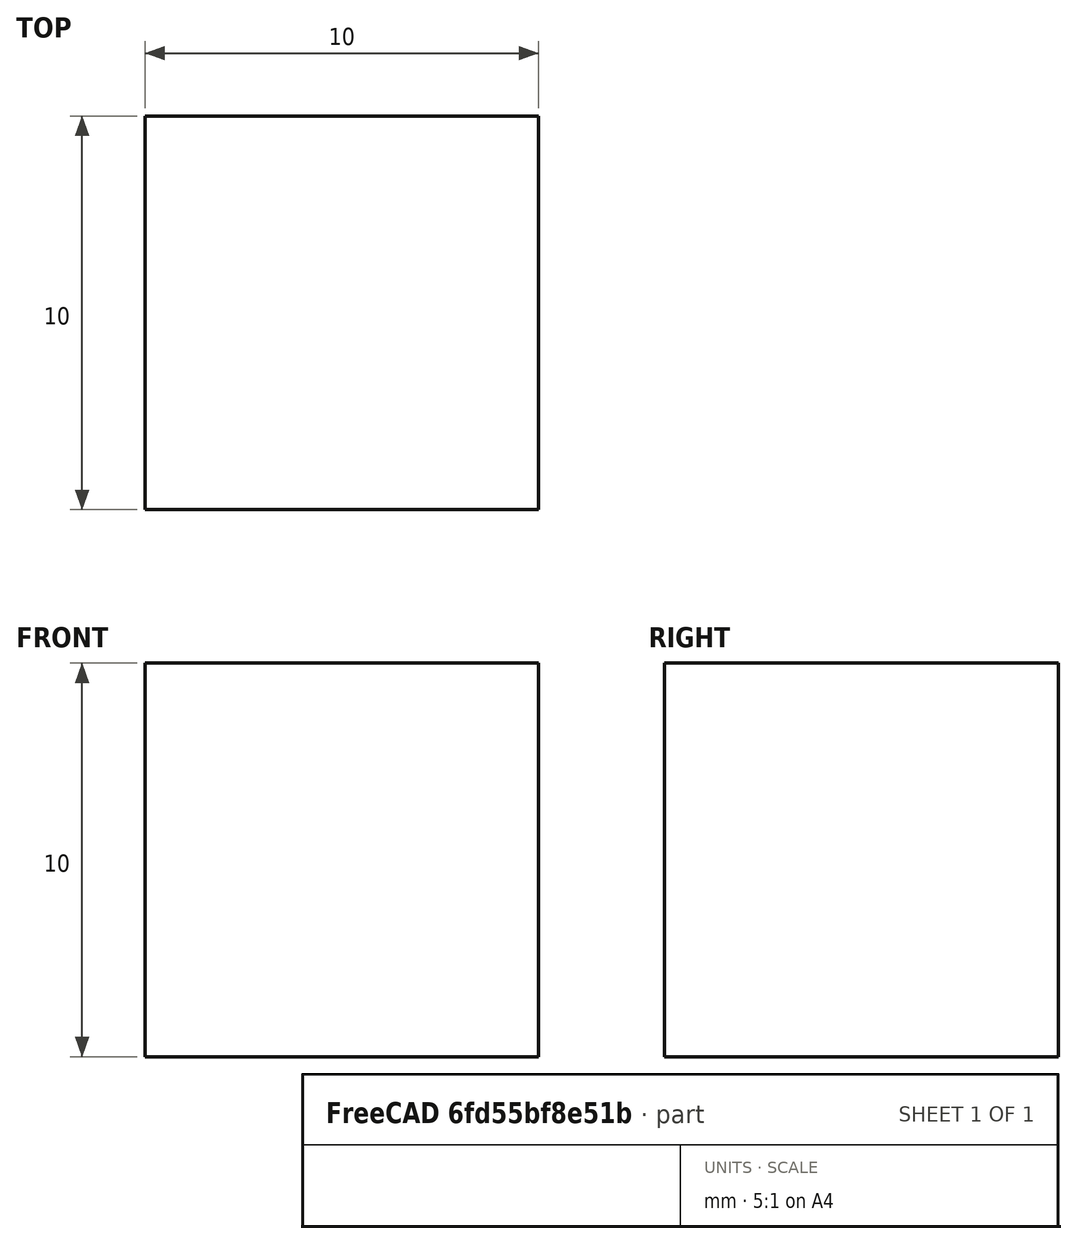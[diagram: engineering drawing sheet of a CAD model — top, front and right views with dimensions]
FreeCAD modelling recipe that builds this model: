
FCSTD DOCUMENT  (FreeCAD 1.0R39109 (Git))
Label: Simple Shear
License: All rights reserved
LicenseURL: http://en.wikipedia.org/wiki/All_rights_reserved
objects: Fem::ConstraintForce×4, Fem::ConstraintDisplacement×2, Part::Box×1, Fem::FemSolverObjectPython×1, App::MaterialObjectPython×1, Fem::FemMeshObjectPython×1, Fem::ConstraintFixed×1, Fem::FemAnalysis×1
note: 1 computed .brp shape members not serialized (recipe doc carries the construction recipe); baked Part::Feature solids carry a one-line shape summary decoded from their .brp

FEATURE [Part::Box] Box  label="Cube"
  AttacherType = Attacher::AttachEngine3D
  Height = 10
  Length = 10
  Width = 10
FEATURE [Fem::FemSolverObjectPython] SolverCcxTools  # FEM object (typed FeaturePython)
  AnalysisType = 0
  BeamReducedIntegration = true
  BeamShellResultOutput3D = false
  BucklingFactors = 1
  EigenmodeHighLimit = 1000000
  EigenmodeLowLimit = 0
  EigenmodesCount = 10
  GeometricalNonlinearity = 0
  IterationsControlParameterCutb = 0.25,0.5,0.75,0.85,,,1.5,
  IterationsControlParameterIter = 4,8,9,200,10,400,,200,,
  IterationsControlParameterTimeUse = false
  IterationsMaximum = 2000
  IterationsUserDefinedIncrementations = false
  IterationsUserDefinedTimeStepLength = false
  MaterialNonlinearity = 0
  MatrixSolverType = 0
  ModelSpace = 0
  OutputFrequency = 1
  SplitInputWriter = false
  ThermoMechSteadyState = true
  ThermoMechType = 0
  TimeEnd = 1
  TimeInitialStep = 0.01
  TimeMaximumStep = 1
  TimeMinimumStep = 1e-05
FEATURE [App::MaterialObjectPython] MaterialSolid  # material (typed FeaturePython)
  Category = 0
  Material = AuthorAndLicense=(c) 2013 Yorik van Havre (CC-BY 3.0); CardName=Concrete-Generic; CompressiveStrength=25 MPa; Density=2400 kg/m^3; Description=A standard C-25 construction concrete; Father=Aggregate; Name=Concrete; PoissonRatio=0.17; ProductURL=https://en.wikipedia.org/wiki/Concrete; StandardCode=Masterformat 03 33 13; YoungsModulus=32000 MPa
FEATURE [Fem::FemMeshObjectPython] FEMMeshGmsh  # FEM object (typed FeaturePython)
  Algorithm2D = 0
  Algorithm3D = 0
  CharacteristicLengthMax = 0
  CharacteristicLengthMin = 10
  CoherenceMesh = true
  ElementDimension = 0
  ElementOrder = 1
  GeometryTolerance = 1e-06
  GroupsOfNodes = false
  HighOrderOptimize = 0
  MeshSizeFromCurvature = 12
  OptimizeNetgen = false
  OptimizeStd = true
  RecombinationAlgorithm = 0
  Recombine3DAll = false
  RecombineAll = false
  SecondOrderLinear = false
  Shape = -> Box
  SubdivisionAlgorithm = 0
FEATURE [Fem::ConstraintForce] ConstraintForce
  Direction = -> Box [Edge10]
  DirectionVector = (1,0,0)
  Force = 100000
  NormalDirection = (0,0,1)
  Normals = (9) [(0,0,1),(0,0,1),(0,0,1),(0,0,1),(0,0,1),(0,0,1),(0,0,1),(0,0,1),(0,0,1)]
  Points = (9) [(0,0,10),(5,0,10),(10,0,10),(0,5,10),(5,5,10),(10,5,10),(0,10,10),(5,10,10),(10,10,10)]
  References = -> [Box]
  Suppressed = false
FEATURE [Fem::ConstraintForce] ConstraintForce001
  Direction = -> Box [Edge5]
  DirectionVector = (0,0,1)
  Force = 100000
  NormalDirection = (1,0,0)
  Normals = (9) [(1,0,0),(1,0,0),(1,0,0),(1,0,0),(1,0,0),(1,0,0),(1,0,0),(1,0,0),(1,0,0)]
  Points = (9) [(10,10,0),(10,10,5),(10,10,10),(10,5,0),(10,5,5),(10,5,10),(10,0,0),(10,0,5),(10,0,10)]
  References = -> [Box]
  Suppressed = false
FEATURE [Fem::ConstraintForce] ConstraintForce002
  Direction = -> Box [Edge1]
  DirectionVector = (0,0,-1)
  Force = 100000
  NormalDirection = (-1,0,0)
  Normals = (9) [(-1,0,0),(-1,0,0),(-1,0,0),(-1,0,0),(-1,0,0),(-1,0,0),(-1,0,0),(-1,0,0),(-1,0,0)]
  Points = (9) [(0,10,0),(0,10,5),(0,10,10),(0,5,0),(0,5,5),(0,5,10),(0,0,0),(0,0,5),(0,0,10)]
  References = -> [Box]
  Reversed = true
  Suppressed = false
FEATURE [Fem::ConstraintForce] ConstraintForce003
  Direction = -> Box [Edge9]
  DirectionVector = (-1,0,0)
  Force = 100000
  NormalDirection = (0,0,-1)
  Normals = (9) [(0,0,-1),(0,0,-1),(0,0,-1),(0,0,-1),(0,0,-1),(0,0,-1),(0,0,-1),(0,0,-1),(0,0,-1)]
  Points = (9) [(0,0,0),(5,0,0),(10,0,0),(0,5,0),(5,5,0),(10,5,0),(0,10,0),(5,10,0),(10,10,0)]
  References = -> [Box]
  Reversed = true
  Suppressed = false
FEATURE [Fem::ConstraintFixed] ConstraintFixed
  NormalDirection = (0,0,1)
  Normals = (1) [(0,0,1)]
  Points = (1) [(0,0,0)]
  References = -> [Box]
  Suppressed = false
FEATURE [Fem::ConstraintDisplacement] ConstraintDisplacement
  NormalDirection = (0,0,1)
  Normals = (1) [(0,0,1)]
  Points = (1) [(0,10,0)]
  References = -> [Box]
  Suppressed = false
  hasXFormula = false
  hasYFormula = false
  hasZFormula = false
  rotxFree = true
  rotyFree = true
  rotzFree = true
  useFlowSurfaceForce = false
  xDisplacement = 0
  xFree = false
  xRotation = 0
  yDisplacement = 0
  yFree = true
  yRotation = 0
  zDisplacement = 0
  zFree = false
  zRotation = 0
FEATURE [Fem::ConstraintDisplacement] ConstraintDisplacement001
  NormalDirection = (0,0,1)
  Normals = (1) [(0,0,1)]
  Points = (1) [(10,0,0)]
  References = -> [Box]
  Suppressed = false
  hasXFormula = false
  hasYFormula = false
  hasZFormula = false
  rotxFree = true
  rotyFree = true
  rotzFree = true
  useFlowSurfaceForce = false
  xDisplacement = 0
  xFree = true
  xRotation = 0
  yDisplacement = 0
  yFree = true
  yRotation = 0
  zDisplacement = 0
  zFree = false
  zRotation = 0
FEATURE [Fem::FemAnalysis] Analysis
  Group = -> [SolverCcxTools,MaterialSolid,FEMMeshGmsh,ConstraintForce,ConstraintForce001,ConstraintForce002,ConstraintForce003,ConstraintFixed,ConstraintDisplacement,ConstraintDisplacement001]
